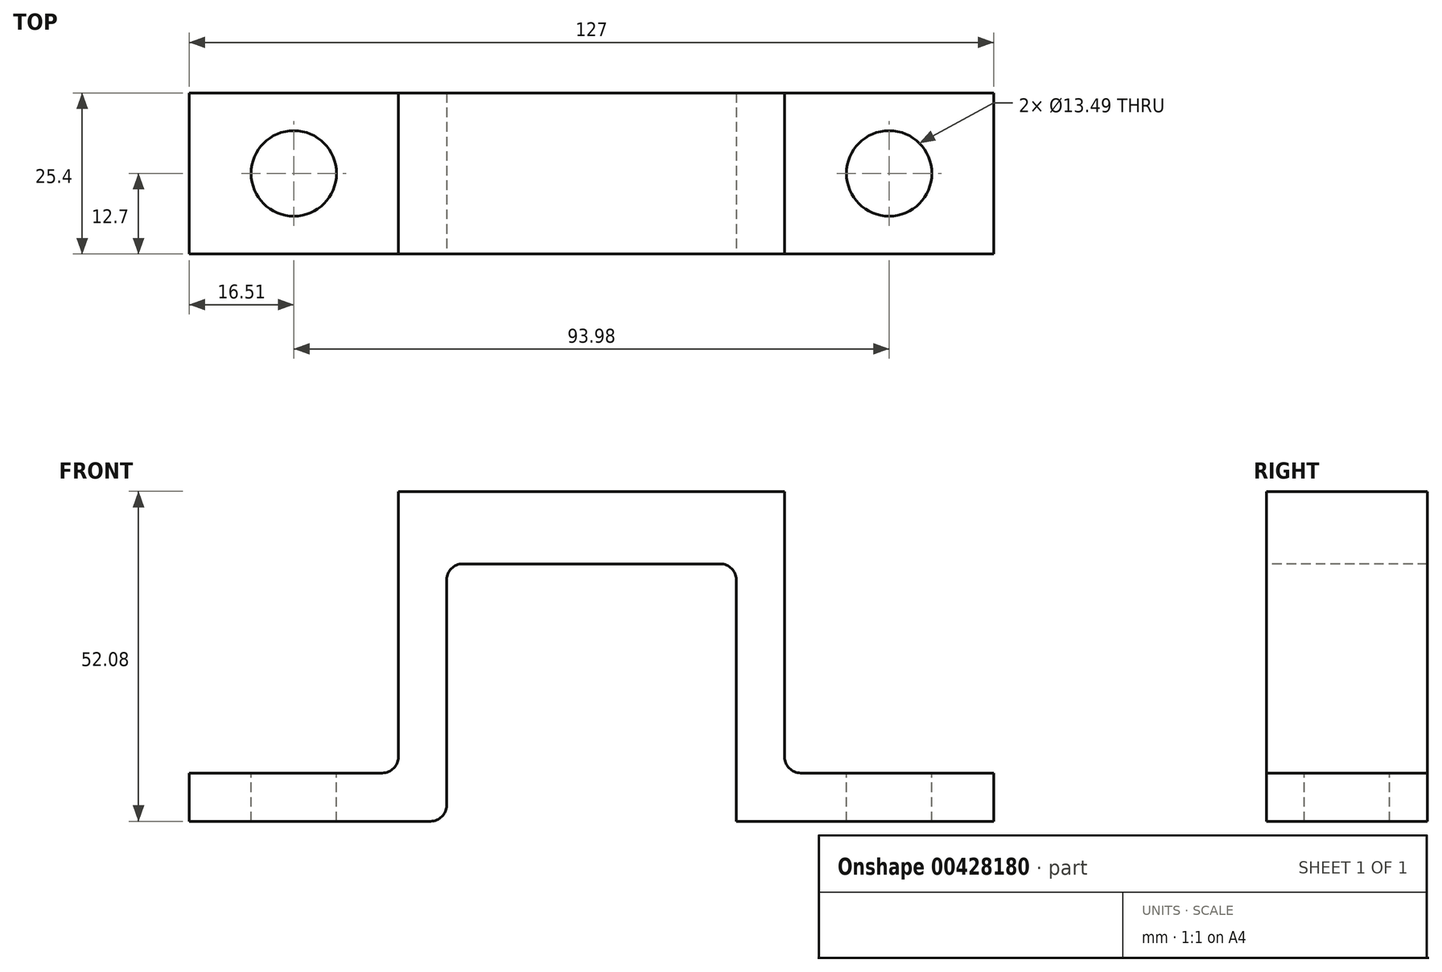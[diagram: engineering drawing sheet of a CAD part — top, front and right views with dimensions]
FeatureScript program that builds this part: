
annotation { "Feature Type Name" : "Feature", "Feature Type Description" : "" }
export const myFeature = defineFeature(function(context is Context, id is Id, definition is map)
    precondition{}
    {
        {
            var Q0;
            Q0=qCreatedBy(makeId("Front.planeOp"),FACE);
            var sketch = newSketch(context, id + "F0", { "sketchPlane" : qUnion([Q0])});
            skLineSegment(sketch, "E0.bottom", {"start": v(63.5, -26.03) * mm, "end": v(-63.5, -26.04) * mm});
            skLineSegment(sketch, "E0.top", {"start": v(63.5, 26.04) * mm, "end": v(-63.5, 26.04) * mm});
            skLineSegment(sketch, "E0.left", {"start": v(63.5, -26.03) * mm, "end": v(63.5, 26.04) * mm});
            skLineSegment(sketch, "E0.right", {"start": v(-63.5, -26.04) * mm, "end": v(-63.5, 26.03) * mm});
            skPoint(sketch, "E0.middle", {"position": v(0, 0) * mm});
            skSolve(sketch);
        }
        {
            var Q0;
            Q0=makeQuery(id+"F0.imprint","IMPRINT",FACE,{"disambiguationData":[TD([[makeQuery(id+"F0.imprint","IMPRINT",EDGE,{"derivedFrom":sQuery(id+"F0.wireOp",EDGE,"E0.bottom")}),-1.0]])]});
            extrude(context, id + "F1", {"entities" : qUnion([Q0]), "endBound" : BoundingType.SYMMETRIC, "depth" : 25.4 * mm});
        }
        {
            var Q0;
            Q0=makeQuery(id+"F1.opExtrude","SWEPT_FACE",FACE,{"disambiguationData":[OSD([sQuery(id+"F0.wireOp",EDGE,"E0.bottom")])]});
            var sketch = newSketch(context, id + "F2", { "sketchPlane" : qUnion([Q0])});
            skLineSegment(sketch, "E1.bottom", {"start": v(22.86, -12.7) * mm, "end": v(-22.86, -12.7) * mm});
            skLineSegment(sketch, "E1.top", {"start": v(22.86, 12.7) * mm, "end": v(-22.86, 12.7) * mm});
            skLineSegment(sketch, "E1.left", {"start": v(22.86, -12.7) * mm, "end": v(22.86, 12.7) * mm});
            skLineSegment(sketch, "E1.right", {"start": v(-22.86, -12.7) * mm, "end": v(-22.86, 12.7) * mm});
            skPoint(sketch, "E1.middle", {"position": v(0, 0) * mm});
            skSolve(sketch);
        }
        {
            var Q0;
            Q0=makeQuery(id+"F2.imprint","IMPRINT",FACE,{"disambiguationData":[TD([[makeQuery(id+"F2.imprint","IMPRINT",EDGE,{"derivedFrom":sQuery(id+"F2.wireOp",EDGE,"E1.bottom")}),-1.0]])]});
            extrude(context, id + "F3", {"entities" : qUnion([Q0]), "operationType" : NewBodyOperationType.REMOVE, "oppositeDirection" : true, "depth" : 40.64 * mm});
        }
        {
            var Q0;
            Q0=makeQuery(id+"F3.boolean.opBoolean","COPY",EDGE,{"derivedFrom":makeQuery(id+"F3.opExtrude","CAP_EDGE",EDGE,{"disambiguationData":[OSD([sQuery(id+"F2.wireOp",EDGE,"E1.right")])],"isStart":false})});
            var Q1;
            Q1=makeQuery(id+"F3.boolean.opBoolean","COPY",EDGE,{"derivedFrom":makeQuery(id+"F3.opExtrude","CAP_EDGE",EDGE,{"disambiguationData":[OSD([sQuery(id+"F2.wireOp",EDGE,"E1.left")])],"isStart":false})});
            fillet(context, id + "F4", {"entities" : qUnion([Q0, Q1]), "radius" : 2.54 * mm, "tangentPropagation" : true, "allowEdgeOverflow" : false});
        }
        {
            var Q0;
            Q0=makeQuery(id+"F1.opExtrude","SWEPT_FACE",FACE,{"disambiguationData":[OSD([sQuery(id+"F0.wireOp",EDGE,"E0.top")])]});
            var sketch = newSketch(context, id + "F5", { "sketchPlane" : qUnion([Q0])});
            skPoint(sketch, "E2", {"position": v(-47, 0) * mm});
            skLineSegment(sketch, "E3.bottom", {"start": v(-63.5, 12.7) * mm, "end": v(-30.48, 12.7) * mm});
            skLineSegment(sketch, "E3.top", {"start": v(-63.5, -12.7) * mm, "end": v(-30.48, -12.7) * mm});
            skLineSegment(sketch, "E3.left", {"start": v(-63.5, 12.7) * mm, "end": v(-63.5, -12.7) * mm});
            skLineSegment(sketch, "E3.right", {"start": v(-30.48, 12.7) * mm, "end": v(-30.48, -12.7) * mm});
            skLineSegment(sketch, "E4.MirrorCS", {"start": v(30.48, 12.7) * mm, "end": v(30.48, -12.7) * mm});
            skLineSegment(sketch, "E5.MirrorCS", {"start": v(63.5, 12.7) * mm, "end": v(30.48, 12.7) * mm});
            skLineSegment(sketch, "E6.MirrorCS", {"start": v(63.5, 12.7) * mm, "end": v(63.5, -12.7) * mm});
            skLineSegment(sketch, "E7.MirrorCS", {"start": v(63.5, -12.7) * mm, "end": v(30.48, -12.7) * mm});
            skPoint(sketch, "E8.MirrorP", {"position": v(47, 0) * mm});
            skSolve(sketch);
        }
        {
            var Q0;
            Q0=makeQuery(id+"F5.imprint","IMPRINT",FACE,{"disambiguationData":[TD([[makeQuery(id+"F5.imprint","IMPRINT",EDGE,{"derivedFrom":sQuery(id+"F5.wireOp",EDGE,"E3.bottom")}),1.0]])]});
            var Q1;
            Q1=makeQuery(id+"F5.imprint","IMPRINT",FACE,{"disambiguationData":[TD([[makeQuery(id+"F5.imprint","IMPRINT",EDGE,{"derivedFrom":sQuery(id+"F5.wireOp",EDGE,"E4.MirrorCS")}),1.0]])]});
            extrude(context, id + "F6", {"entities" : qUnion([Q0, Q1]), "operationType" : NewBodyOperationType.REMOVE, "oppositeDirection" : true, "depth" : 44.45 * mm});
        }
        {
            var Q0;
            Q0=makeQuery(id+"F6.boolean.opBoolean","COPY",EDGE,{"derivedFrom":makeQuery(id+"F6.opExtrude","CAP_EDGE",EDGE,{"disambiguationData":[OSD([sQuery(id+"F5.wireOp",EDGE,"E3.right")])],"isStart":false})});
            var Q1;
            Q1=makeQuery(id+"F6.boolean.opBoolean","COPY",EDGE,{"derivedFrom":makeQuery(id+"F6.opExtrude","CAP_EDGE",EDGE,{"disambiguationData":[OSD([sQuery(id+"F5.wireOp",EDGE,"E4.MirrorCS")])],"isStart":false})});
            var Q2;
            Q2=makeQuery(id+"F3.boolean.opBoolean","COPY",EDGE,{"derivedFrom":makeQuery(id+"F3.opExtrude","CAP_EDGE",EDGE,{"disambiguationData":[OSD([sQuery(id+"F2.wireOp",EDGE,"E1.right")])],"isStart":true})});
            var Q3;
            Q3=makeQuery(id+"F3.boolean.opBoolean","COPY",EDGE,{"derivedFrom":makeQuery(id+"F3.opExtrude","CAP_EDGE",EDGE,{"disambiguationData":[OSD([sQuery(id+"F2.wireOp",EDGE,"E1.left")])],"isStart":true})});
            fillet(context, id + "F7", {"entities" : qUnion([Q0, Q1, Q2, Q3]), "radius" : 2.54 * mm, "tangentPropagation" : true, "allowEdgeOverflow" : false});
        }
        {
            var Q0;
            Q0=sQuery(id+"F5.wireOp",VERTEX,"E2");
            var Q1;
            Q1=sQuery(id+"F5.wireOp",VERTEX,"E8.MirrorP");
            var Q2;
            Q2=makeQuery(id+"F1.opExtrude","SWEPT_BODY",BODY,{"disambiguationData":[OSD([sQuery(id+"F0.wireOp",EDGE,"E0.bottom"),sQuery(id+"F0.wireOp",EDGE,"E0.top"),sQuery(id+"F0.wireOp",EDGE,"E0.left"),sQuery(id+"F0.wireOp",EDGE,"E0.right")])]});
            hole(context, id + "F8", {"style" : HoleStyle.SIMPLE, "endStyle" : HoleEndStyle.THROUGH, "standardTappedOrClearance" : lookupTablePath({ "standard" : "ANSI", "fit" : "Normal (ASME)", "size" : "1/2", "type" : "Clearance" }), "standardBlindInLast" : lookupTablePath({ "fit" : "Free", "standard" : "ANSI", "size" : "1/2", "type" : "Clearance" }), "holeDiameter" : 13.5 * mm, "tappedDepth" : 19.54 * mm, "tapClearance" : 3, "startFromSketch" : true, "locations" : qUnion([Q0, Q1]), "scope" : qUnion([Q2])});
        }
    });
